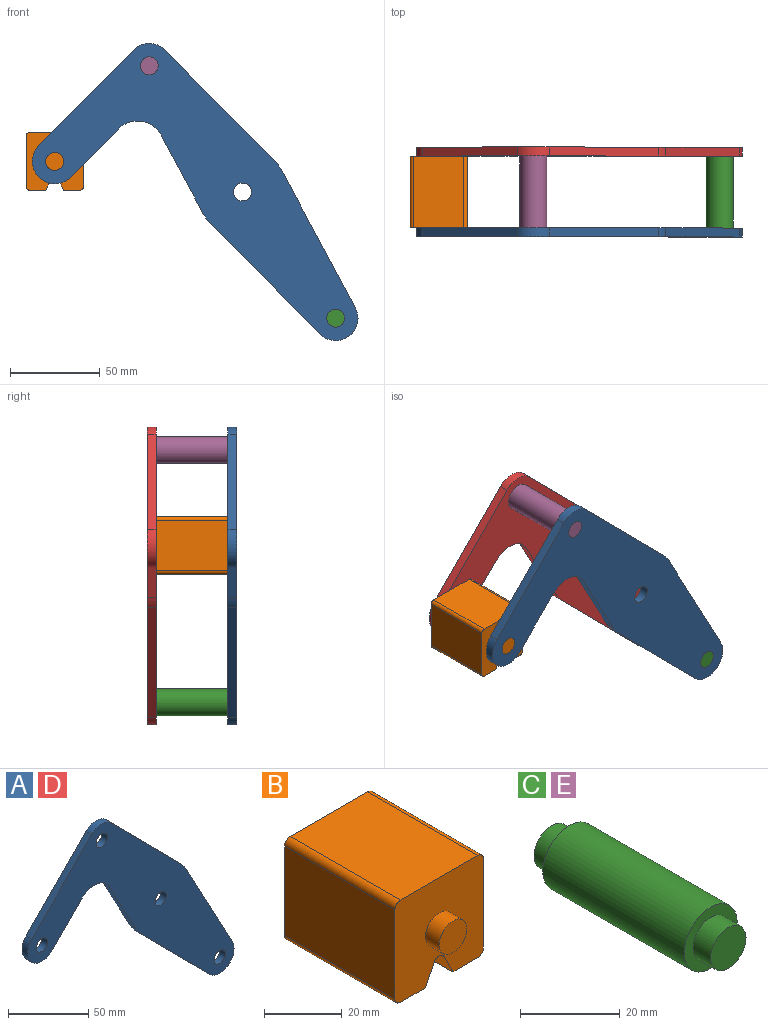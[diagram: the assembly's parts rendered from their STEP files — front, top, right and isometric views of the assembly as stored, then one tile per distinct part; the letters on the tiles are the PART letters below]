
ASSEMBLY  parts=5 mates=3
PART A: 18 faces, bbox 181.7x5x165.8 mm
  f0: plane 43.49x23.35mm, normal (-0.88,0,-0.47), area 246.8mm2, adj f1,f14,f16,f17
  f1: cylinder r=25mm len=5.75mm, axis (0,1,0), area 35.8mm2, adj f0,f2,f16,f17
  f2: plane 61.6x60.87mm, normal (-0.71,0,-0.7), area 433mm2, adj f1,f3,f16,f17
  f3: cylinder r=12.5mm len=21.39mm, axis (0,1,0), area 178.4mm2, adj f2,f4,f16,f17
  f4: plane 76.3x40.96mm, normal (0.88,0,0.47), area 433mm2, adj f3,f5,f16,f17
  f5: cylinder r=25mm len=5.75mm, axis (0,1,0), area 35.8mm2, adj f4,f6,f16,f17
  f6: plane 61.6x60.87mm, normal (0.71,0,0.7), area 433mm2, adj f5,f7,f16,f17
  f7: cylinder r=12.5mm len=17.78mm, axis (0,1,0), area 98.9mm2, adj f6,f8,f16,f17
  f8: plane 53.35x52.71mm, normal (-0.71,0,0.7), area 375mm2, adj f7,f9,f16,f17
  f9: cylinder r=12.5mm len=21.39mm, axis (0,1,0), area 196.3mm2, adj f8,f10,f16,f17
  f10: plane 26.86x26.54mm, normal (0.71,0,-0.7), area 188.8mm2, adj f9,f14,f16,f17
  f11: cylinder r=5mm len=10mm, axis (0,1,0), area 157.1mm2, adj f16,f17
  f12: cylinder r=5mm len=10mm, axis (0,1,0), area 157.1mm2, adj f16,f17
  f13: cylinder r=5mm len=10mm, axis (0,1,0), area 157.1mm2, adj f16,f17
  f14: cylinder r=15mm len=23.89mm, axis (0,1,0), area 140.2mm2, adj f0,f10,f16,f17
  f15: cylinder r=5mm len=10mm, axis (0,1,0), area 157.1mm2, adj f16,f17
  f16: plane 181.66x165.78mm, normal (0,-1,0), area 8710.1mm2, adj f0,f1,f2,f3,f4,f5,f6,f7
  f17: plane 181.66x165.78mm, normal (0,1,0), area 8710.1mm2, adj f0,f1,f2,f3,f4,f5,f6,f7
PART B: 18 faces, bbox 32.1x50x32.1 mm
  f0: plane 40x28.08mm, normal (1,0,0), area 1123.1mm2, adj f4,f10,f13,f14
  f1: plane 40x9.04mm, normal (0,0,-1), area 361.6mm2, adj f2,f4,f10,f14
  f2: plane 40x6.42mm, normal (-0.89,0,-0.45), area 287.2mm2, adj f1,f4,f10,f15
  f3: plane 40x6.42mm, normal (0.89,0,-0.45), area 287.2mm2, adj f4,f5,f10,f15
  f4: plane 32.08x32.08mm, normal (0,-1,0), area 900.6mm2, adj f0,f1,f2,f3,f5,f6,f7,f9
  f5: plane 40x9.04mm, normal (0,0,-1), area 361.6mm2, adj f3,f4,f10,f16
  f6: plane 40x28.08mm, normal (0,0,1), area 1123.1mm2, adj f4,f10,f13,f17
  f7: plane 40x28.08mm, normal (-1,0,0), area 1123.1mm2, adj f4,f10,f16,f17
  f8: plane 10x10mm, normal (0,-1,0), area 78.5mm2, adj f9
  f9: cylinder r=5mm len=10mm, axis (0,1,0), area 157.1mm2, adj f4,f8
  f10: plane 32.08x32.08mm, normal (0,1,0), area 900.6mm2, adj f0,f1,f2,f3,f5,f6,f7,f12
  f11: plane 10x10mm, normal (0,1,0), area 78.5mm2, adj f12
  f12: cylinder r=5mm len=10mm, axis (0,-1,0), area 157.1mm2, adj f10,f11
  f13: cylinder r=2mm len=40mm, axis (0,1,0), area 125.7mm2, adj f0,f4,f6,f10
  f14: cylinder r=2mm len=40mm, axis (0,-1,0), area 125.7mm2, adj f0,f1,f4,f10
  f15: cylinder r=2mm len=40mm, axis (0,1,0), area 177.1mm2, adj f2,f3,f4,f10
  f16: cylinder r=2mm len=40mm, axis (0,1,0), area 125.7mm2, adj f4,f5,f7,f10
  f17: cylinder r=2mm len=40mm, axis (0,-1,0), area 125.7mm2, adj f4,f6,f7,f10
PART C: 7 faces, bbox 15x50x15 mm
  f0: cylinder r=7.5mm len=40mm, axis (0,-1,0), area 1885mm2, adj f2,f5
  f1: cylinder r=5mm len=10mm, axis (0,1,0), area 157.1mm2, adj f2,f3
  f2: plane 15x15mm, normal (0,-1,0), area 98.2mm2, adj f0,f1
  f3: plane 10x10mm, normal (0,-1,0), area 78.5mm2, adj f1
  f4: cylinder r=5mm len=10mm, axis (0,-1,0), area 157.1mm2, adj f5,f6
  f5: plane 15x15mm, normal (0,1,0), area 98.2mm2, adj f0,f4
  f6: plane 10x10mm, normal (0,1,0), area 78.5mm2, adj f4
PART D: same geometry as A
PART E: same geometry as C
PLACE A t=(0,-15,0)mm fixed
PLACE B t=(0,-15,0)mm
PLACE C t=(103.95,-15,-140.78)mm
PLACE D t=(0,30,0)mm
PLACE E t=(0,-15,0)mm
MATE revolute A.f9 <-> B.f9  axis (0,1,0) through (-104.69,-15,17.04)mm
MATE fastened C.f0 <-> A.f3  axis (0,-1,0) through (51.98,-15,-70.39)mm
MATE revolute D.f7 <-> E.f0  axis (0,-1,0) through (-51.98,25,70.39)mm
